MODEL helikoptera_model
KIND model
BLOCK [Constant] Constant1
  OutDataType = fixdt(1, 16)
  OutScaling = 2^0
  SID = 102
  Value = 0
BLOCK [Constant] Constant2
  OutDataType = fixdt(1, 16)
  OutScaling = 2^0
  SID = 101
  Value = 0
BLOCK [Constant] Constant3
  OutDataType = fixdt(1, 16)
  OutScaling = 2^0
  SID = 103
  Value = 0
BLOCK [Gain] Gain
  Gain = Kcelk
  Multiplication = Matrix(K*u)
  OutDataType = fixdt(1, 16)
  OutDataTypeMode = Inherit via internal rule
  OutDataTypeStr = Inherit: Inherit via internal rule
  OutScaling = 2^0
  ParamDataTypeStr = Inherit: Inherit via internal rule
  ParameterDataType = fixdt(1, 16)
  ParameterDataTypeMode = Inherit via internal rule
  ParameterScaling = 2^0
  SID = 89
  SaturateOnIntegerOverflow = off
BLOCK [Gain] Gain1
  Gain = sys_stav.C
  Multiplication = Matrix(K*u)
  OutDataType = fixdt(1, 16)
  OutDataTypeMode = Inherit via internal rule
  OutDataTypeStr = Inherit: Inherit via internal rule
  OutScaling = 2^0
  ParamDataTypeStr = Inherit: Inherit via internal rule
  ParameterDataType = fixdt(1, 16)
  ParameterDataTypeMode = Inherit via internal rule
  ParameterScaling = 2^0
  SID = 90
  SaturateOnIntegerOverflow = off
BLOCK [Mux] Mux
  DisplayOption = bar
  Ports = [4, 1]
  SID = 97
BLOCK [Reference] PID Controller  REF=simulink/Continuous/PID Controller
  AntiWindupMode = none
  Controller = PID
  D = 0.01
  DOutDataTypeStr = Inherit: Inherit via internal rule
  DOutMax = []
  DOutMin = []
  DParamDataTypeStr = Inherit: Inherit via internal rule
  DParamMax = []
  DParamMin = []
  DialogController = pidpack.PIDConfig.pidDDGCreate
  DialogControllerArgs = DataTag0
  ExternalReset = none
  FilterContinuousStateAttributes = ''
  FilterMethod = Forward Euler
  FilterOutDataTypeStr = Inherit: Inherit via internal rule
  FilterOutMax = []
  FilterOutMin = []
  FilterRTWStateStorageClass = Auto
  FilterStateMustResolveToSignalObject = off
  Form = Parallel
  FunctionWithSeparateData = off
  I = 0.0001
  IOutDataTypeStr = Inherit: Inherit via internal rule
  IOutMax = []
  IOutMin = []
  IParamDataTypeStr = Inherit: Inherit via internal rule
  IParamMax = []
  IParamMin = []
  IgnoreLimit = off
  InitialConditionForFilter = 0
  InitialConditionForIntegrator = 0
  InitialConditionSource = internal
  IntegratorContinuousStateAttributes = ''
  IntegratorMethod = Forward Euler
  IntegratorOutDataTypeStr = Inherit: Inherit via internal rule
  IntegratorOutMax = []
  IntegratorOutMin = []
  IntegratorRTWStateStorageClass = Auto
  IntegratorStateMustResolveToSignalObject = off
  Kb = 1
  KbOutDataTypeStr = Inherit: Inherit via internal rule
  KbOutMax = []
  KbOutMin = []
  KbParamDataTypeStr = Inherit: Inherit via internal rule
  KbParamMax = []
  KbParamMin = []
  Kt = 1
  KtOutDataTypeStr = Inherit: Inherit via internal rule
  KtOutMax = []
  KtOutMin = []
  KtParamDataTypeStr = Inherit: Inherit via internal rule
  KtParamMax = []
  KtParamMin = []
  LimitOutput = off
  LinearizeAsGain = off
  LockScale = off
  LowerSaturationLimit = -inf
  N = 100
  NOutDataTypeStr = Inherit: Inherit via internal rule
  NOutMax = []
  NOutMin = []
  NParamDataTypeStr = Inherit: Inherit via internal rule
  NParamMax = []
  NParamMin = []
  P = 1e-06
  POutDataTypeStr = Inherit: Inherit via internal rule
  POutMax = []
  POutMin = []
  PParamDataTypeStr = Inherit: Inherit via internal rule
  PParamMax = []
  PParamMin = []
  Ports = [1, 1]
  RTWMemSecDataConstants = Inherit from model
  RTWMemSecDataInternal = Inherit from model
  RTWMemSecDataParameters = Inherit from model
  RTWMemSecFuncExecute = Inherit from model
  RTWMemSecFuncInitTerm = Inherit from model
  RndMeth = Floor
  SID = 76
  SampleTime = 1
  SaturateOnIntegerOverflow = off
  SaturationOutDataTypeStr = Inherit: Same as input
  SaturationOutMax = []
  SaturationOutMin = []
  ShowPortLabels = FromPortIcon
  SourceBlock = simulink/Continuous/PID Controller
  SourceType = PID 1dof
  SumAccumDataTypeStr = Inherit: Inherit via internal rule
  SumDAccumDataTypeStr = Inherit: Inherit via internal rule
  SumDOutDataTypeStr = Inherit: Inherit via internal rule
  SumDOutMax = []
  SumDOutMin = []
  SumI1AccumDataTypeStr = Inherit: Inherit via internal rule
  SumI1OutDataTypeStr = Inherit: Inherit via internal rule
  SumI1OutMax = []
  SumI1OutMin = []
  SumI2AccumDataTypeStr = Inherit: Inherit via internal rule
  SumI2OutDataTypeStr = Inherit: Inherit via internal rule
  SumI2OutMax = []
  SumI2OutMin = []
  SumI3AccumDataTypeStr = Inherit: Inherit via internal rule
  SumI3OutDataTypeStr = Inherit: Inherit via internal rule
  SumI3OutMax = []
  SumI3OutMin = []
  SumOutDataTypeStr = Inherit: Inherit via internal rule
  SumOutMax = []
  SumOutMin = []
  SystemSampleTime = -1
  TimeDomain = Continuous-time
  TrackingMode = off
  UpperSaturationLimit = inf
  ZeroCross = on
BLOCK [Scope] Scope
  DataFormat = StructureWithTime
  Floating = off
  NumInputPorts = 1
  Ports = [1]
  SID = 1
  SampleTime = 0
  TimeRange = 2
  YMax = 0.9425
  YMin = 0.9335
BLOCK [Scope] Scope2
  DataFormat = StructureWithTime
  Floating = off
  NumInputPorts = 1
  Ports = [1]
  SID = 78
  SampleTime = 0
  SaveName = ScopeData2
  TimeRange = 2
  YMax = 40
  YMin = -20
BLOCK [Scope] Scope4
  DataFormat = StructureWithTime
  Floating = off
  NumInputPorts = 1
  Ports = [1]
  SID = 91
  SampleTime = 0
  SaveName = ScopeData1
  YMax = 8e-06
  YMin = 0
BLOCK [StateSpace] State-Space1
  A = Gnew.a
  B = Gnew.b
  C = Gnew.c
  D = Gnew.d
  SID = 80
BLOCK [StateSpace] State-Space2
  A = sys.a
  B = sys.b
  C = sys.c
  D = sys.d
  SID = 27
BLOCK [StateSpace] State-Space3
  A = sys_stav.a
  B = sys_stav.b
  C = eye(4)
  D = [0 0 0 0]'
  SID = 92
BLOCK [Step] Step
  After = 10
  SID = 3
  SampleTime = 0
  Time = 0
BLOCK [Step] Step1
  After = 10
  SID = 81
  SampleTime = 0
  Time = 0
BLOCK [Step] Step2
  After = 10
  SID = 93
  SampleTime = 0
  Time = 0
BLOCK [Sum] Sum
  IconShape = round
  InputSameDT = off
  Inputs = |+-
  OutDataType = fixdt(1, 16)
  OutDataTypeMode = Inherit via internal rule
  OutDataTypeStr = Inherit: Inherit via internal rule
  OutScaling = 2^0
  Ports = [2, 1]
  SID = 5
  SaturateOnIntegerOverflow = off
BLOCK [Sum] Sum1
  IconShape = round
  InputSameDT = off
  Inputs = ++|
  OutDataType = fixdt(1, 16)
  OutDataTypeMode = Inherit via internal rule
  OutDataTypeStr = Inherit: Inherit via internal rule
  OutScaling = 2^0
  Ports = [2, 1]
  SID = 88
  SaturateOnIntegerOverflow = off
BLOCK [Sum] Sum2
  IconShape = round
  InputSameDT = off
  Inputs = |+-
  OutDataType = fixdt(1, 16)
  OutDataTypeMode = Inherit via internal rule
  OutDataTypeStr = Inherit: Inherit via internal rule
  OutScaling = 2^0
  Ports = [2, 1]
  SID = 94
  SaturateOnIntegerOverflow = off
BLOCK [Sum] Sum3
  IconShape = round
  InputSameDT = off
  Inputs = |++
  OutDataType = fixdt(1, 16)
  OutDataTypeMode = Inherit via internal rule
  OutDataTypeStr = Inherit: Inherit via internal rule
  OutScaling = 2^0
  Ports = [2, 1]
  SID = 105
  SaturateOnIntegerOverflow = off
BLOCK [UniformRandomNumber] Uniform Random\nNumber
  Maximum = 0.5
  Minimum = -0.5
  SID = 87
  SampleTime = 0.1
BLOCK [UniformRandomNumber] Uniform Random\nNumber1
  Maximum = 0.1
  Minimum = -0.1
  SID = 104
  SampleTime = 0.1
ANNOTATION (root): 
LINE Constant1:1 -> Mux:3
LINE Constant2:1 -> Mux:4
LINE Constant3:1 -> Mux:1
LINE Gain1:1 -> Scope4:1
LINE Gain:1 -> Sum2:2
LINE Mux:1 -> Sum3:2
LINE PID Controller:1 -> State-Space2:1
LINE State-Space1:1 -> Scope2:1
LINE State-Space2:1 -> Sum1:2
NET State-Space3:1 -> Gain1:1, Sum3:1
LINE Step1:1 -> State-Space1:1
LINE Step2:1 -> Sum2:1
LINE Step:1 -> Sum:1
NET Sum1:1 -> Scope:1, Sum:2
LINE Sum2:1 -> State-Space3:1
LINE Sum3:1 -> Gain:1
LINE Sum:1 -> PID Controller:1
LINE Uniform Random\nNumber1:1 -> Mux:2
LINE Uniform Random\nNumber:1 -> Sum1:1
note: NET lines group one-source signal fan-out (src -> all destinations, sorted); 1:1 wires keep LINE
